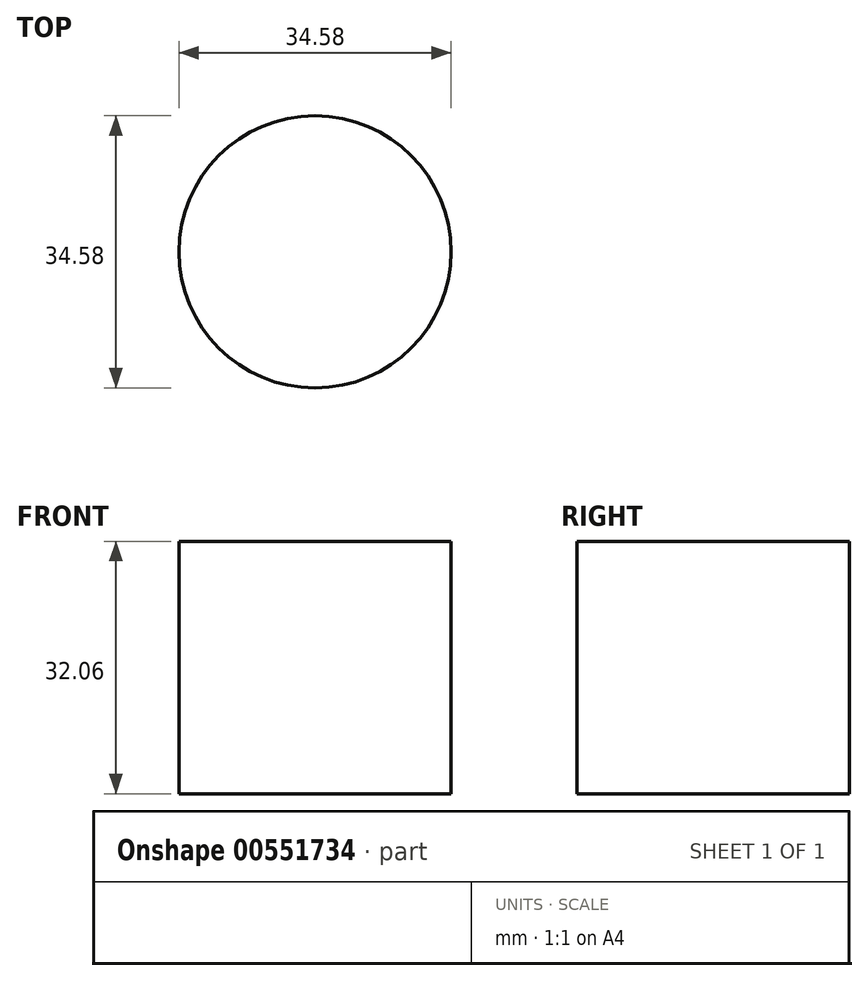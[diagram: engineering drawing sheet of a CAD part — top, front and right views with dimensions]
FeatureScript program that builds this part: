
annotation { "Feature Type Name" : "Feature", "Feature Type Description" : "" }
export const myFeature = defineFeature(function(context is Context, id is Id, definition is map)
    precondition{}
    {
        {
            var Q0;
            Q0=qCreatedBy(makeId("Front.planeOp"),FACE);
            var sketch = newSketch(context, id + "F0", { "sketchPlane" : qUnion([Q0])});
            skLineSegment(sketch, "E0.bottom", {"start": v(0, 32.06) * mm, "end": v(17.29, 32.06) * mm});
            skLineSegment(sketch, "E0.top", {"start": v(0, 0) * mm, "end": v(17.29, 0) * mm});
            skLineSegment(sketch, "E0.left", {"start": v(0, 32.06) * mm, "end": v(0, 0) * mm});
            skLineSegment(sketch, "E0.right", {"start": v(17.29, 32.06) * mm, "end": v(17.29, 0) * mm});
            skLineSegment(sketch, "E1", {"start": v(0, 43.59) * mm, "end": v(0, -19.36) * mm, "construction": true});
            skPoint(sketch, "E1.endSnap0", {"position": v(0, 16.03) * mm});
            skSolve(sketch);
        }
        {
            var Q0;
            Q0 = qSketchRegion(id + "F0", true);
            var Q1;
            Q1=sQuery(id+"F0.wireOp",EDGE,"E1");
            revolve(context, id + "F1", {"entities" : qUnion([Q0]), "axis" : qUnion([Q1]), "revolveType" : RevolveType.FULL});
        }
    });
